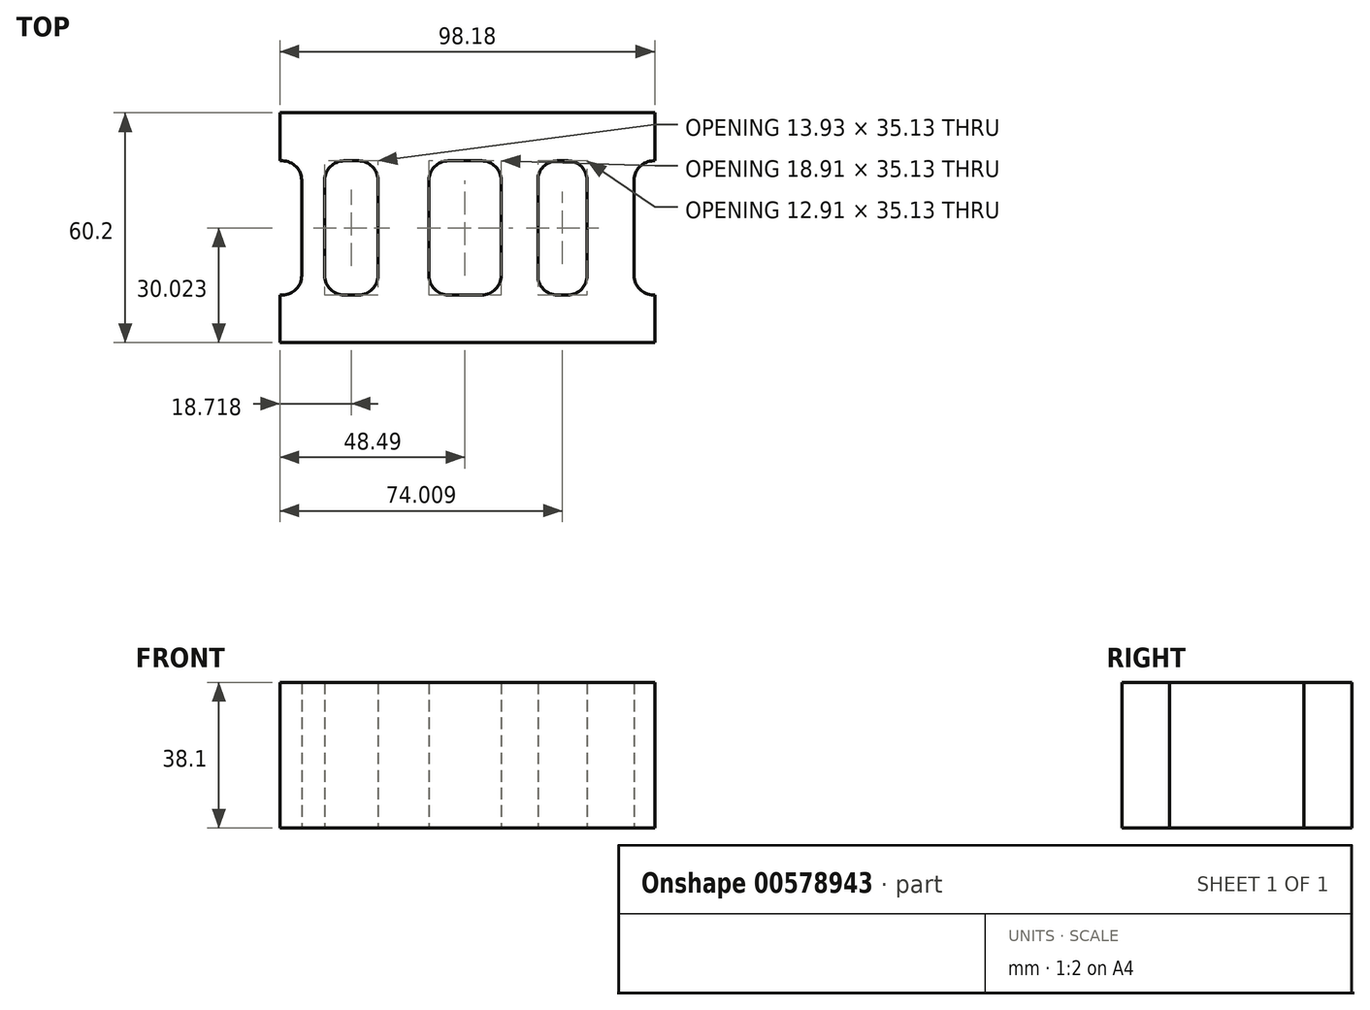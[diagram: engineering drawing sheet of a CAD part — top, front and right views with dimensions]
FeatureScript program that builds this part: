
annotation { "Feature Type Name" : "Feature", "Feature Type Description" : "" }
export const myFeature = defineFeature(function(context is Context, id is Id, definition is map)
    precondition{}
    {
        {
            var Q0;
            Q0=qCreatedBy(makeId("Top.planeOp"),FACE);
            var sketch = newSketch(context, id + "F0", { "sketchPlane" : qUnion([Q0])});
            skLineSegment(sketch, "E0", {"start": v(-48.94, 0) * mm, "end": v(49.24, 0) * mm});
            skLineSegment(sketch, "E1", {"start": v(49.24, 0) * mm, "end": v(49.24, 12.46) * mm});
            skLineSegment(sketch, "E2", {"start": v(49.24, 12.46) * mm, "end": v(48.91, 12.46) * mm});
            skLineSegment(sketch, "E3", {"start": v(43.83, 17.54) * mm, "end": v(43.83, 42.5) * mm});
            skLineSegment(sketch, "E4", {"start": v(48.91, 47.59) * mm, "end": v(49.24, 47.59) * mm});
            skLineSegment(sketch, "E5", {"start": v(49.24, 47.59) * mm, "end": v(49.24, 60.2) * mm});
            skLineSegment(sketch, "E6", {"start": v(49.24, 60.2) * mm, "end": v(-48.94, 60.2) * mm});
            skLineSegment(sketch, "E7", {"start": v(-48.94, 60.2) * mm, "end": v(-48.94, 47.59) * mm});
            skLineSegment(sketch, "E8", {"start": v(-48.94, 47.59) * mm, "end": v(-48.31, 47.59) * mm});
            skLineSegment(sketch, "E9", {"start": v(-43.23, 42.5) * mm, "end": v(-43.23, 17.54) * mm});
            skLineSegment(sketch, "E10", {"start": v(-48.31, 12.46) * mm, "end": v(-48.94, 12.46) * mm});
            skLineSegment(sketch, "E11", {"start": v(-48.94, 12.46) * mm, "end": v(-48.94, 0) * mm});
            skLineSegment(sketch, "E12", {"start": v(-37.19, 42.5) * mm, "end": v(-37.19, 17.54) * mm});
            skLineSegment(sketch, "E13", {"start": v(-32.1, 12.46) * mm, "end": v(-28.34, 12.46) * mm});
            skLineSegment(sketch, "E14", {"start": v(-23.26, 17.54) * mm, "end": v(-23.26, 42.5) * mm});
            skLineSegment(sketch, "E15", {"start": v(-28.34, 47.59) * mm, "end": v(-32.1, 47.59) * mm});
            skLineSegment(sketch, "E16", {"start": v(-9.9, 42.5) * mm, "end": v(-9.9, 17.54) * mm});
            skLineSegment(sketch, "E17", {"start": v(-4.83, 12.46) * mm, "end": v(3.93, 12.46) * mm});
            skLineSegment(sketch, "E18", {"start": v(9, 17.54) * mm, "end": v(9, 42.5) * mm});
            skLineSegment(sketch, "E19", {"start": v(3.93, 47.59) * mm, "end": v(-4.83, 47.59) * mm});
            skLineSegment(sketch, "E20", {"start": v(18.61, 42.5) * mm, "end": v(18.61, 17.54) * mm});
            skLineSegment(sketch, "E21", {"start": v(23.7, 12.46) * mm, "end": v(26.44, 12.46) * mm});
            skLineSegment(sketch, "E22", {"start": v(31.52, 17.54) * mm, "end": v(31.52, 42.5) * mm});
            skLineSegment(sketch, "E23", {"start": v(26.44, 47.59) * mm, "end": v(23.7, 47.59) * mm});
            skPoint(sketch, "E24.visualSharp", {"position": v(-37.19, 47.59) * mm});
            skArc(sketch, "E24.filletArc", {"start": v(-32.1, 47.59) * mm, "mid": v(-35.7, 46.1) * mm, "end": v(-37.19, 42.5) * mm});
            skPoint(sketch, "E25.visualSharp", {"position": v(-23.26, 47.59) * mm});
            skArc(sketch, "E25.filletArc", {"start": v(-23.26, 42.5) * mm, "mid": v(-24.74, 46.1) * mm, "end": v(-28.34, 47.59) * mm});
            skPoint(sketch, "E26.visualSharp", {"position": v(-23.26, 12.46) * mm});
            skArc(sketch, "E26.filletArc", {"start": v(-28.34, 12.46) * mm, "mid": v(-24.74, 13.95) * mm, "end": v(-23.26, 17.54) * mm});
            skPoint(sketch, "E27.visualSharp", {"position": v(-37.19, 12.46) * mm});
            skArc(sketch, "E27.filletArc", {"start": v(-37.19, 17.54) * mm, "mid": v(-35.7, 13.95) * mm, "end": v(-32.1, 12.46) * mm});
            skPoint(sketch, "E28.visualSharp", {"position": v(9, 47.59) * mm});
            skArc(sketch, "E28.filletArc", {"start": v(9, 42.5) * mm, "mid": v(7.52, 46.1) * mm, "end": v(3.93, 47.59) * mm});
            skPoint(sketch, "E29.visualSharp", {"position": v(9, 12.46) * mm});
            skArc(sketch, "E29.filletArc", {"start": v(3.93, 12.46) * mm, "mid": v(7.52, 13.95) * mm, "end": v(9, 17.54) * mm});
            skPoint(sketch, "E30.visualSharp", {"position": v(-9.9, 12.46) * mm});
            skArc(sketch, "E30.filletArc", {"start": v(-9.9, 17.54) * mm, "mid": v(-8.42, 13.95) * mm, "end": v(-4.83, 12.46) * mm});
            skPoint(sketch, "E31.visualSharp", {"position": v(-9.9, 47.59) * mm});
            skArc(sketch, "E31.filletArc", {"start": v(-4.83, 47.59) * mm, "mid": v(-8.42, 46.1) * mm, "end": v(-9.9, 42.5) * mm});
            skPoint(sketch, "E32.visualSharp", {"position": v(18.61, 47.59) * mm});
            skArc(sketch, "E32.filletArc", {"start": v(23.7, 47.59) * mm, "mid": v(20.1, 46.1) * mm, "end": v(18.61, 42.5) * mm});
            skPoint(sketch, "E33.visualSharp", {"position": v(18.61, 12.46) * mm});
            skArc(sketch, "E33.filletArc", {"start": v(18.61, 17.54) * mm, "mid": v(20.1, 13.95) * mm, "end": v(23.7, 12.46) * mm});
            skPoint(sketch, "E34.visualSharp", {"position": v(31.52, 12.46) * mm});
            skArc(sketch, "E34.filletArc", {"start": v(26.44, 12.46) * mm, "mid": v(30.04, 13.95) * mm, "end": v(31.52, 17.54) * mm});
            skPoint(sketch, "E35.visualSharp", {"position": v(31.52, 47.59) * mm});
            skArc(sketch, "E35.filletArc", {"start": v(31.52, 42.5) * mm, "mid": v(30.04, 46.1) * mm, "end": v(26.44, 47.59) * mm});
            skPoint(sketch, "E36.visualSharp", {"position": v(-43.23, 47.59) * mm});
            skArc(sketch, "E36.filletArc", {"start": v(-43.23, 42.5) * mm, "mid": v(-44.72, 46.1) * mm, "end": v(-48.31, 47.59) * mm});
            skPoint(sketch, "E37.visualSharp", {"position": v(-43.23, 12.46) * mm});
            skArc(sketch, "E37.filletArc", {"start": v(-48.31, 12.46) * mm, "mid": v(-44.72, 13.95) * mm, "end": v(-43.23, 17.54) * mm});
            skPoint(sketch, "E38.visualSharp", {"position": v(43.83, 12.46) * mm});
            skArc(sketch, "E38.filletArc", {"start": v(43.83, 17.54) * mm, "mid": v(45.32, 13.95) * mm, "end": v(48.91, 12.46) * mm});
            skPoint(sketch, "E39.visualSharp", {"position": v(43.83, 47.59) * mm});
            skArc(sketch, "E39.filletArc", {"start": v(48.91, 47.59) * mm, "mid": v(45.32, 46.1) * mm, "end": v(43.83, 42.5) * mm});
            skSolve(sketch);
        }
        {
            var Q0;
            Q0 = qSketchRegion(id + "F0", true);
            extrude(context, id + "F1", {"entities" : qUnion([Q0]), "depth" : 38.1 * mm, "offsetDistance" : 25.4 * mm});
        }
    });
